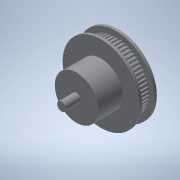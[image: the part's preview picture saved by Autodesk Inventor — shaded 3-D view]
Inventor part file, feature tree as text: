
AUTODESK INVENTOR PART (.ipt)
format: ipt  version: 2022 (Build 260153000, 153)  size: 271,872 bytes
history: native  units: mm
features: sketch x5, extrude x4, revolve x1, pattern_circular x1
ambient origin geometry x8: Origin, YZ Plane, XZ Plane, XY Plane, X Axis, Y Axis, Z Axis, Center Point
bodies: Solid1 (feature_tree)
feature tree (11):
  revolve  "Revolution1"  [1 undecoded]
  extrude  "Extrusion1"  Depth=18.95mm
  pattern_circular  "Circular Pattern1"  [2 undecoded]
  extrude  "Extrusion2"  Depth=8.65mm TaperAngle=360.0deg
  extrude  "Extrusion3"  Depth=22.0mm
  extrude  "Extrusion4"  Depth=8.65mm
  sketch  "Sketch1"  dims[d0=4.0mm d1=7.0mm]
  sketch  "Sketch2"  dims[d4=1.5mm d6=18.95mm]
  sketch  "Sketch3"  dims[d7=90.0deg]
  sketch  "Sketch4"  dims[d8=1.3mm]
  sketch  "Sketch5"  dims[d9=18.85mm d10=10.0mm d11=0.0mm d12=600.0mm d13=360.0deg d15=22.0mm d16=6.0mm d17=12.5mm d18=7.5mm d19=16.0mm d20=0.0mm d21=0.0mm d22=8.0mm d23=0.0mm d24=5.0mm d25=8.65mm d26=0.0mm]
note: 3 required parameter values undecoded (feature->parameter linkage not recoverable at this tier; creation-order binding heuristic only, values carry confidence <= 0.55)